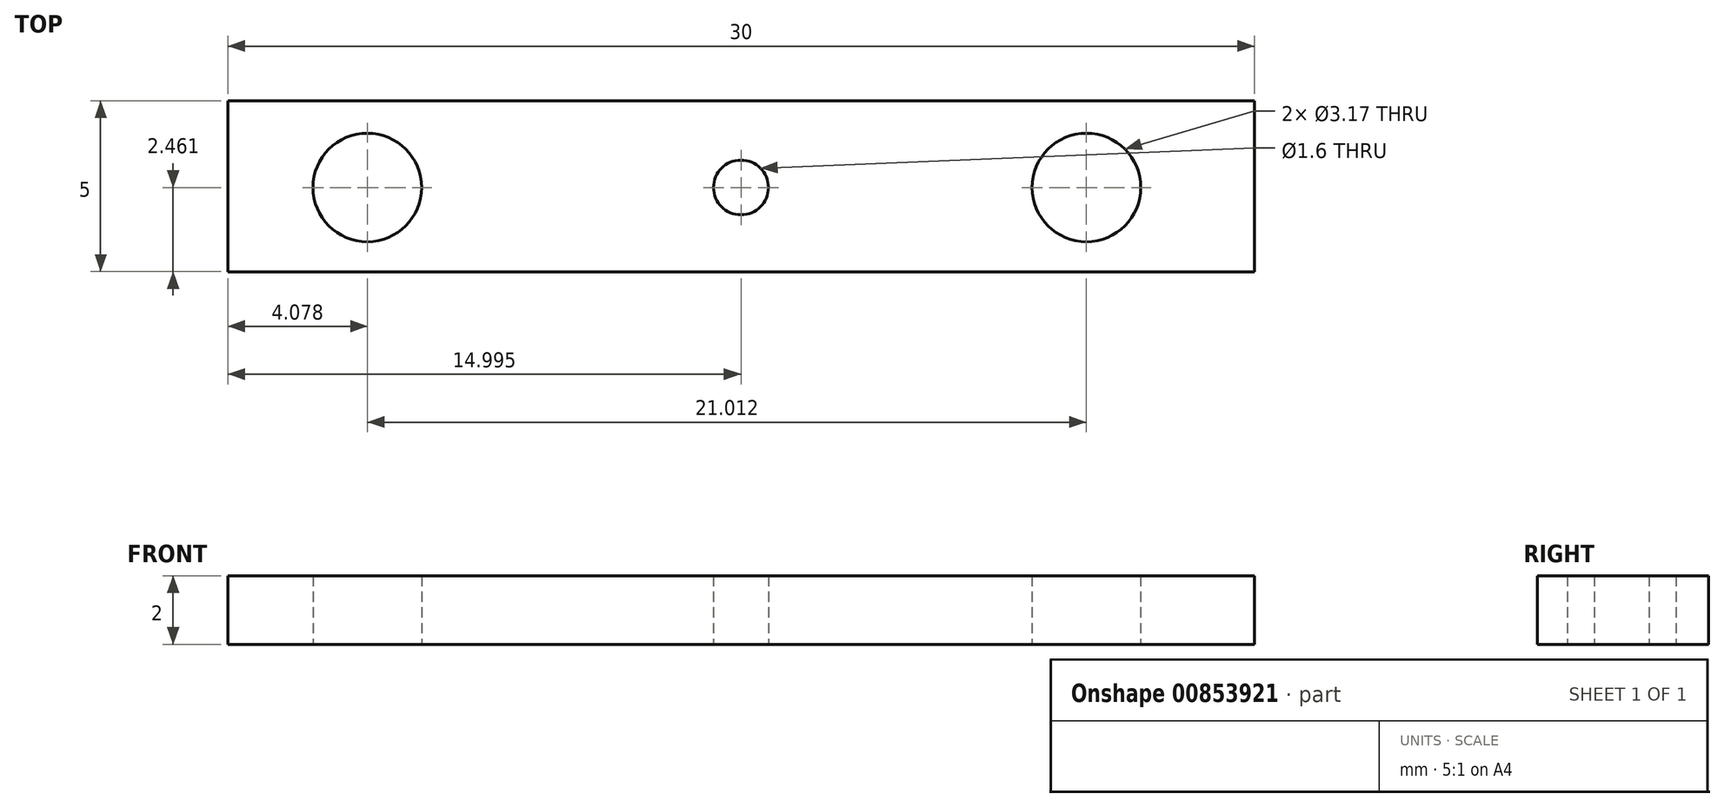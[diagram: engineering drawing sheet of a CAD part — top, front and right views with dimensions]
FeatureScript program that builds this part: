
annotation { "Feature Type Name" : "Feature", "Feature Type Description" : "" }
export const myFeature = defineFeature(function(context is Context, id is Id, definition is map)
    precondition{}
    {
        {
            var Q0;
            Q0=qCreatedBy(makeId("Top.planeOp"),FACE);
            var sketch = newSketch(context, id + "F0", { "sketchPlane" : qUnion([Q0])});
            skLineSegment(sketch, "E0.bottom", {"start": v(-37.83, -1.53) * mm, "end": v(-7.83, -1.53) * mm});
            skLineSegment(sketch, "E0.top", {"start": v(-37.83, -6.53) * mm, "end": v(-7.83, -6.53) * mm});
            skLineSegment(sketch, "E0.left", {"start": v(-37.83, -1.53) * mm, "end": v(-37.83, -6.53) * mm});
            skLineSegment(sketch, "E0.right", {"start": v(-7.83, -1.53) * mm, "end": v(-7.83, -6.53) * mm});
            skCircle(sketch, "E1", {"center": v(-22.83, -4.07) * mm, "radius": 0.8 * mm});
            skCircle(sketch, "E2", {"center": v(-33.75, -4.07) * mm, "radius": 1.59 * mm});
            skCircle(sketch, "E3", {"center": v(-12.74, -4.07) * mm, "radius": 1.59 * mm});
            skSolve(sketch);
        }
        {
            var Q0;
            Q0=makeQuery(id+"F0.imprint","IMPRINT",FACE,{"disambiguationData":[TD([[makeQuery(id+"F0.imprint","IMPRINT",EDGE,{"derivedFrom":sQuery(id+"F0.wireOp",EDGE,"E0.bottom")}),-1.0]])]});
            extrude(context, id + "F1", {"entities" : qUnion([Q0]), "depth" : 2 * mm, "offsetDistance" : 25.4 * mm});
        }
    });
